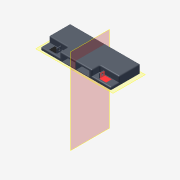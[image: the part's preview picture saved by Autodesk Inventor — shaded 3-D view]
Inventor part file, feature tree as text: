
AUTODESK INVENTOR PART (.ipt)
format: ipt  version: 2016 SP1 (Build 200210100, 210)  size: 364,032 bytes
history: native  units: mm (DEFAULTED — no unit token found)
features: sketch x10, extrude x9, fillet x5, plane x5, mirror x3, split x3, hole x1
ambient origin geometry x8: Origin, YZ Plane, XZ Plane, XY Plane, X Axis, Y Axis, Z Axis, Center Point
bodies: Solid1 (feature_tree)
feature tree (36):
  extrude  "Extrusion1"  Depth=74.422mm
  extrude  "Extrusion2"  Depth=139.7mm TaperAngle=0.0deg
  extrude  "Extrusion3"  Depth=21.336mm
  fillet  "Fillet1"  Radius=14.224mm
  fillet  "Fillet3"  Radius=2.54mm
  fillet  "Fillet4"  Radius=2.54mm
  extrude  "Extrusion4"  Depth=0.254mm TaperAngle=0.0deg
  extrude  "Extrusion5"  Depth=12.7mm TaperAngle=0.0deg
  extrude  "Extrusion6"  Depth=12.7mm TaperAngle=0.0deg
  plane  "Work Plane1"
  mirror  "Mirror1"
  mirror  "Mirror2"
  extrude  "Extrusion7"  Depth=20.32mm
  extrude  "Extrusion8"  Depth=19.558mm TaperAngle=0.0deg
  plane  "Work Plane2"
  fillet  "Fillet5"  Radius=33.02mm
  plane  "Work Plane3"
  extrude  "Extrusion9"  Depth=19.05mm TaperAngle=0.0deg
  hole  "Hole1"  [1 undecoded]
  fillet  "Fillet6"  Radius=56.261mm
  mirror  "Mirror3"
  plane  "Work Plane4"
  split  "Split2"
  plane  "Work Plane6"
  split  "Split3"
  split  "Split4"
  sketch  "Sketch1"  dims[d0=179.578mm d1=74.422mm]
  sketch  "Sketch2"  dims[d2=139.7mm d3=0.0mm d4=21.082mm d5=0.0mm]
  sketch  "Sketch3"  dims[d6=49.276mm d7=21.336mm d8=14.224mm d9=0.0mm d10=2.54mm d12=2.54mm]
  sketch  "Sketch4"  dims[d13=2.54mm d14=0.254mm d15=0.0mm]
  sketch  "Sketch5"  dims[d16=1.524mm d17=12.7mm d18=0.0mm]
  sketch  "Sketch6"  dims[d19=5.08mm d20=12.7mm d21=0.0mm]
  sketch  "Sketch7"  dims[d22=20.32mm d23=20.32mm]
  sketch  "Sketch8"  dims[d24=63.5mm d25=19.558mm d26=0.0mm d27=33.02mm]
  sketch  "Sketch9"  dims[d28=3.048mm d29=19.05mm d30=0.0mm]
  sketch  "Sketch10"  dims[d31=181.102mm d32=-127.0mm d34=1.27mm d35=56.261mm d36=11.9888mm d37=11.5062mm d38=2.0066mm d39=0.0mm d40=5.4864mm d41=5.4864mm d42=19.05mm d43=9.525mm d44=6.35mm d45=14.3117mm d46=25.4mm d47=20.594885mm d48=1.27mm d49=14.986mm d50=90.0deg d51=0.0mm]
note: 1 required parameter value undecoded (feature->parameter linkage not recoverable at this tier; creation-order binding heuristic only, values carry confidence <= 0.55)
